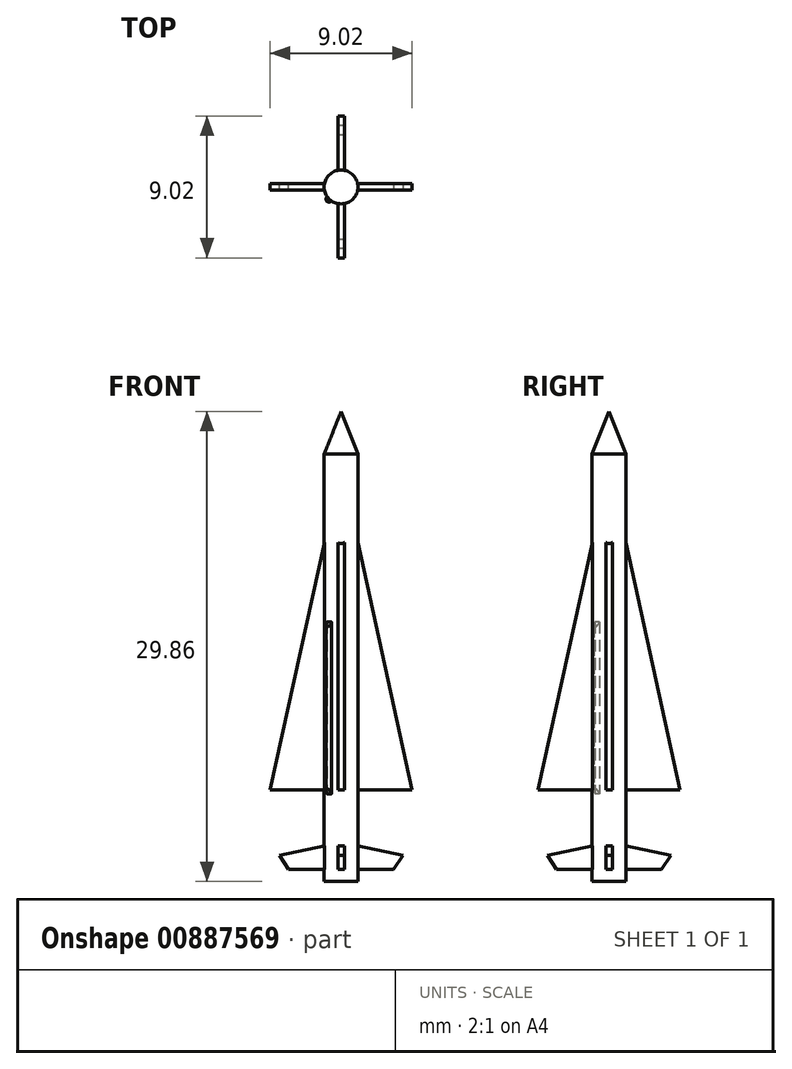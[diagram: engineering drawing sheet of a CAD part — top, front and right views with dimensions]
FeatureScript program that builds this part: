
annotation { "Feature Type Name" : "Feature", "Feature Type Description" : "" }
export const myFeature = defineFeature(function(context is Context, id is Id, definition is map)
    precondition{}
    {
        {
            var Q0;
            Q0=qCreatedBy(makeId("Front.planeOp"),FACE);
            var sketch = newSketch(context, id + "F0", { "sketchPlane" : qUnion([Q0])});
            skLineSegment(sketch, "E0", {"start": v(0, 0) * mm, "end": v(0, 29.86) * mm});
            skLineSegment(sketch, "E1", {"start": v(1.08, 27.15) * mm, "end": v(1.08, 0) * mm});
            skLineSegment(sketch, "E2", {"start": v(1.08, 0) * mm, "end": v(0, 0) * mm});
            skArc(sketch, "E3", {"start": v(0.55, 29.51) * mm, "mid": v(0.32, 29.77) * mm, "end": v(0, 29.86) * mm});
            skArc(sketch, "E4", {"start": v(1.08, 27.15) * mm, "mid": v(0.94, 28.36) * mm, "end": v(0.55, 29.51) * mm});
            skLineSegment(sketch, "E5", {"start": v(0, 29.86) * mm, "end": v(707.3, 29.86) * mm, "construction": true});
            skLineSegment(sketch, "E6", {"start": v(0, 29.86) * mm, "end": v(1.08, 27.15) * mm});
            skSolve(sketch);
        }
        {
            var Q0;
            Q0=makeQuery(id+"F0.imprint","IMPRINT",FACE,{"disambiguationData":[TD([[makeQuery(id+"F0.imprint","IMPRINT",EDGE,{"derivedFrom":sQuery(id+"F0.wireOp",EDGE,"E0")}),-1.0]])]});
            var Q1;
            Q1=sQuery(id+"F0.wireOp",EDGE,"E0");
            revolve(context, id + "F1", {"surfaceOperationType" : NewSurfaceOperationType.NEW, "entities" : qUnion([Q0]), "axis" : qUnion([Q1]), "revolveType" : RevolveType.FULL});
        }
        {
            var Q0;
            Q0=qCreatedBy(makeId("Front.planeOp"),FACE);
            var sketch = newSketch(context, id + "F2", { "sketchPlane" : qUnion([Q0])});
            skLineSegment(sketch, "E7.0", {"start": v(-1.08, 0) * mm, "end": v(1.08, 0) * mm, "construction": true});
            skLineSegment(sketch, "E8", {"start": v(0, 0.76) * mm, "end": v(3.33, 0.76) * mm});
            skLineSegment(sketch, "E9", {"start": v(3.92, 1.67) * mm, "end": v(-1.08, 2.7) * mm});
            skLineSegment(sketch, "E10", {"start": v(0.4, 2.4) * mm, "end": v(0.4, 5.83) * mm});
            skLineSegment(sketch, "E11", {"start": v(0.4, 5.83) * mm, "end": v(4.51, 5.83) * mm});
            skLineSegment(sketch, "E12", {"start": v(4.51, 5.83) * mm, "end": v(0, 26.35) * mm});
            skLineSegment(sketch, "E13", {"start": v(0, 26.35) * mm, "end": v(0, 0.76) * mm});
            skLineSegment(sketch, "E14", {"start": v(-1.08, 0) * mm, "end": v(-1.08, 0) * mm});
            skLineSegment(sketch, "E15", {"start": v(0.4, 2.4) * mm, "end": v(-1.08, 2.7) * mm});
            skLineSegment(sketch, "E16", {"start": v(3.33, 0.76) * mm, "end": v(3.92, 1.67) * mm});
            skLineSegment(sketch, "E17.0", {"start": v(1.08, 27.15) * mm, "end": v(-1.08, 27.15) * mm});
            skLineSegment(sketch, "E18", {"start": v(1.08, 27.15) * mm, "end": v(1.08, 21.46) * mm, "construction": true});
            skSolve(sketch);
        }
        {
            var Q0;
            {var subQ1=sQuery(id+"F2.wireOp",EDGE,"E10");var subQ7=sQuery(id+"F2.wireOp",EDGE,"E8");Q0=qUnion([makeQuery(id+"F2.imprint","IMPRINT",FACE,{"disambiguationData":[TD([[makeQuery(id+"F2.imprint","IMPRINT",EDGE,{"derivedFrom":subQ7}),1.0]])]}),makeQuery(id+"F2.imprint","IMPRINT",FACE,{"disambiguationData":[TD([[makeQuery(id+"F2.imprint","IMPRINT",EDGE,{"derivedFrom":subQ1}),1.0]])]})]);}
            extrude(context, id + "F3", {"entities" : qUnion([Q0]), "operationType" : NewBodyOperationType.ADD, "oppositeDirection" : true, "depth" : .4 * mm, "offsetDistance" : 25 * mm, "symmetric" : true});
        }
        {
            var Q0;
            Q0=makeQuery(id+"F1.opRevolve","SWEPT_BODY",BODY,{"disambiguationData":[OSD([sQuery(id+"F0.wireOp",EDGE,"E0"),sQuery(id+"F0.wireOp",EDGE,"E1"),sQuery(id+"F0.wireOp",EDGE,"E2"),sQuery(id+"F0.wireOp",EDGE,"h1jDSi8t-veb7-85qg-XgDk-6E8DmZjBuz4r")])]});
            var Q1;
            Q1=makeQuery(id+"F1.opRevolve","SWEPT_FACE",FACE,{"disambiguationData":[OSD([sQuery(id+"F0.wireOp",EDGE,"E1")])]});
            circularPattern(context, id + "F4", {"operationType" : NewBodyOperationType.ADD, "entities" : qUnion([Q0]), "axis" : qUnion([Q1]), "angle" : 360 * degree, "instanceCount" : 4, "equalSpace" : true, "computeTransformsWithoutBuiltin" : true});
        }
        {
            var Q0;
            Q0=qCreatedBy(makeId("Top.planeOp"),FACE);
            cPlane(context, id + "F5", {"entities" : qUnion([Q0]), "cplaneType" : CPlaneType.OFFSET, "offset" : 6 * mm, "width" : 150 * mm, "height" : 150 * mm});
        }
        {
            var Q0;
            Q0=qCreatedBy(id+"F5.planeOp",FACE);
            var sketch = newSketch(context, id + "F6", { "sketchPlane" : qUnion([Q0])});
            skLineSegment(sketch, "E19", {"start": v(-0.9, -0.62) * mm, "end": v(-0.7, -0.42) * mm});
            skLineSegment(sketch, "E20", {"start": v(-0.7, -0.42) * mm, "end": v(-0.42, -0.7) * mm});
            skLineSegment(sketch, "E21", {"start": v(-0.42, -0.7) * mm, "end": v(-0.62, -0.9) * mm});
            skArc(sketch, "E22", {"start": v(-0.9, -0.62) * mm, "mid": v(-0.9, -0.9) * mm, "end": v(-0.62, -0.9) * mm});
            skLineSegment(sketch, "E23", {"start": v(-0.57, -0.57) * mm, "end": v(0, 0) * mm, "construction": true});
            skLineSegment(sketch, "E24", {"start": v(0, 0) * mm, "end": v(-0.48, 0) * mm, "construction": true});
            skSolve(sketch);
        }
        {
            var Q0;
            Q0=makeQuery(id+"F6.imprint","IMPRINT",FACE,{"disambiguationData":[TD([[makeQuery(id+"F6.imprint","IMPRINT",EDGE,{"derivedFrom":sQuery(id+"F6.wireOp",EDGE,"E19")}),-1.0]])]});
            extrude(context, id + "F7", {"entities" : qUnion([Q0]), "operationType" : NewBodyOperationType.ADD, "depth" : (1450 / 144) * mm, "offsetDistance" : 25 * mm});
        }
        {
            var Q0;
            Q0=makeQuery(id+"F7.boolean.opBoolean","INTERSECT",EDGE,{"derivedFrom":[makeQuery(id+"F1.opRevolve","SWEPT_FACE",FACE,{"disambiguationData":[OSD([sQuery(id+"F0.wireOp",EDGE,"E1")])]}),makeQuery(id+"F7.opExtrude","CAP_FACE",FACE,{"disambiguationData":[OSD([sQuery(id+"F6.wireOp",EDGE,"E19"),sQuery(id+"F6.wireOp",EDGE,"E20"),sQuery(id+"F6.wireOp",EDGE,"E21"),sQuery(id+"F6.wireOp",EDGE,"E22")])],"isStart":false})]});
            var Q1;
            Q1=makeQuery(id+"F7.boolean.opBoolean","INTERSECT",EDGE,{"derivedFrom":[makeQuery(id+"F1.opRevolve","SWEPT_FACE",FACE,{"disambiguationData":[OSD([sQuery(id+"F0.wireOp",EDGE,"E1")])]}),makeQuery(id+"F7.opExtrude","CAP_FACE",FACE,{"disambiguationData":[OSD([sQuery(id+"F6.wireOp",EDGE,"E19"),sQuery(id+"F6.wireOp",EDGE,"E20"),sQuery(id+"F6.wireOp",EDGE,"E21"),sQuery(id+"F6.wireOp",EDGE,"E22")])],"isStart":true})]});
            chamfer(context, id + "F8", {"entities" : qUnion([Q0, Q1]), "chamferType" : ChamferType.OFFSET_ANGLE, "width" : .25 * mm, "oppositeDirection" : true, "angle" : 60 * degree, "tangentPropagation" : true});
        }
    });
